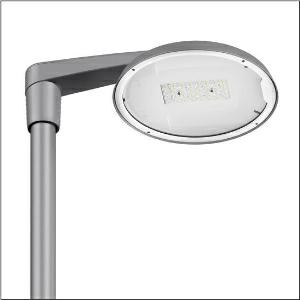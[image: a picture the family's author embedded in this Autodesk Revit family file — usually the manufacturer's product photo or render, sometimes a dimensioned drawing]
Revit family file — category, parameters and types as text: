
# Revit family: dl_r__50_iq_mini___st0_5a_5xa248b41f08he_56c2
name_source: partatom
category: Lighting Fixtures
units: mm (PartAtom-declared; Revit-internal decimal feet)

## family parameters
Cut with Voids When Loaded = No
Host = Face
Light Source = No
Part Type = Normal
Room Calculation Point = No
Round Connector Dimension = Use Diameter
Shared = No

## types (1)
- --- (1 x LED, 9400 lm, 64.6 W, 4000K)
    Apparent Load = 65 VA
    CIE Flux Codes = 41 75 97 100 100
    Color Rendering = 70
    Color Temperature = 4000K
    Default Elevation = 1800 mm
    Description = DL® 50 iQ mini, mast luminaire, primary light control with lens, of PMMA, primary optical cover: cover, of toughened safety glass, transparent, light distribution: ST0.5a, light emission: direct distribution, primary light characteristic: asymmetric, installation type: side-entry, post-top, LED, High Power LED, rated luminous flux: 9.400lm, luminous efficacy: 146lm/W, light colour: 740, colour temperature: 4000K, control: optimised constant luminous flux control (CLO 2.0), Desk-Remote (wireless, voltage-free reading and setting of iQ features in the workshop via application-optimized NFC function/RFID function), Light-Fading, Smart-Wire, Night-Set, Lumen-Switch, Temp-Guard, Auto-Match, Street-Remote, mains connection: 230..240V, AC, 50/60Hz, connection cable pre-assembled, cable length: 8,5m, start of lifetime: 65W, end of service life: 68W, reduction: 29W, luminaire housing, of diecast aluminium, powder-coated, Siteco® metallic grey (DB 702S), inclination adjustable: 0°, 5°, 10° (post-top) | 0°, -5°, -10°, -15° (side-entry), please order mast post-top element or mast side-entry element separately, diameter: 500mm, height: 115mm, post-top: for spigot size d x l = 76 x 100mm; with reducer (optional accessory) 60 x 100mm | side-entry: for spigot size d x l = 60 x 100mm; with reducer (optional accessory) 42 x 100mm, protection rating (complete): IP66, insulation class (complete): insulation class II (safety insulation), certification: CE, ENEC, VDE, impact resistance: IK08, permissible operating ambient temperature for outdoor applications: -25..+40°C, standard-compliant lighting for roads and squares, packaging unit: 1 piece

Light Distribution: ST0.5a
    Height = 115 mm
    Lamp = 1 x LED
    Lamp Light Flux = 9400 lm
    Lamp Power = 64.6 W
    Lamp count = 1
    Length = 500 mm
    Luminous efficacy = 146 lm/W
    Manufacturer = Siteco
    ModVariant = No
    Model = 5XA248B41F08HE
    Number of Poles = 1
    OnlyDefault = Yes
    Power Factor = 1
    Product Name = DL® 50 iQ mini | ST0.5a
    Product group = mast luminaire | pylon top
    ProductGroupID = 6100
    Protection Class = Protection class II
    Protection Degree = IP 66
    RLX_Detail_Level = 1
    RLX_Emergency_Light_Flux = 0 lm
    RLX_Emergency_Type = 0
    RLX_Emergency_Type_DB = No
    RlxData = <blob elided: 126893 chars, md5=92d5a6dc>
    Socket = socket
    Standby Power = 0 W
    System Light Flux = 9400 lm
    System Power = 65 W
    Type Comments = factory setting: luminous flux: 100 % | dim-lin: 254 | 655 mA
    Type Image = l_1251794.jpg
    URL = http://relux.com
    VarID = @adj_092555
    Voltage = 0 V
    Weight = 0.00 kg
    Width = 0 mm  [stored 0 ft]

note: [stored X ft] marks values corroborated as IEEE doubles in the binary element streams (Revit-internal decimal feet)

## geometry (parser evidence)
native form markers: Blend x4, Sweep x12
no freeform markers — native parametric forms only
